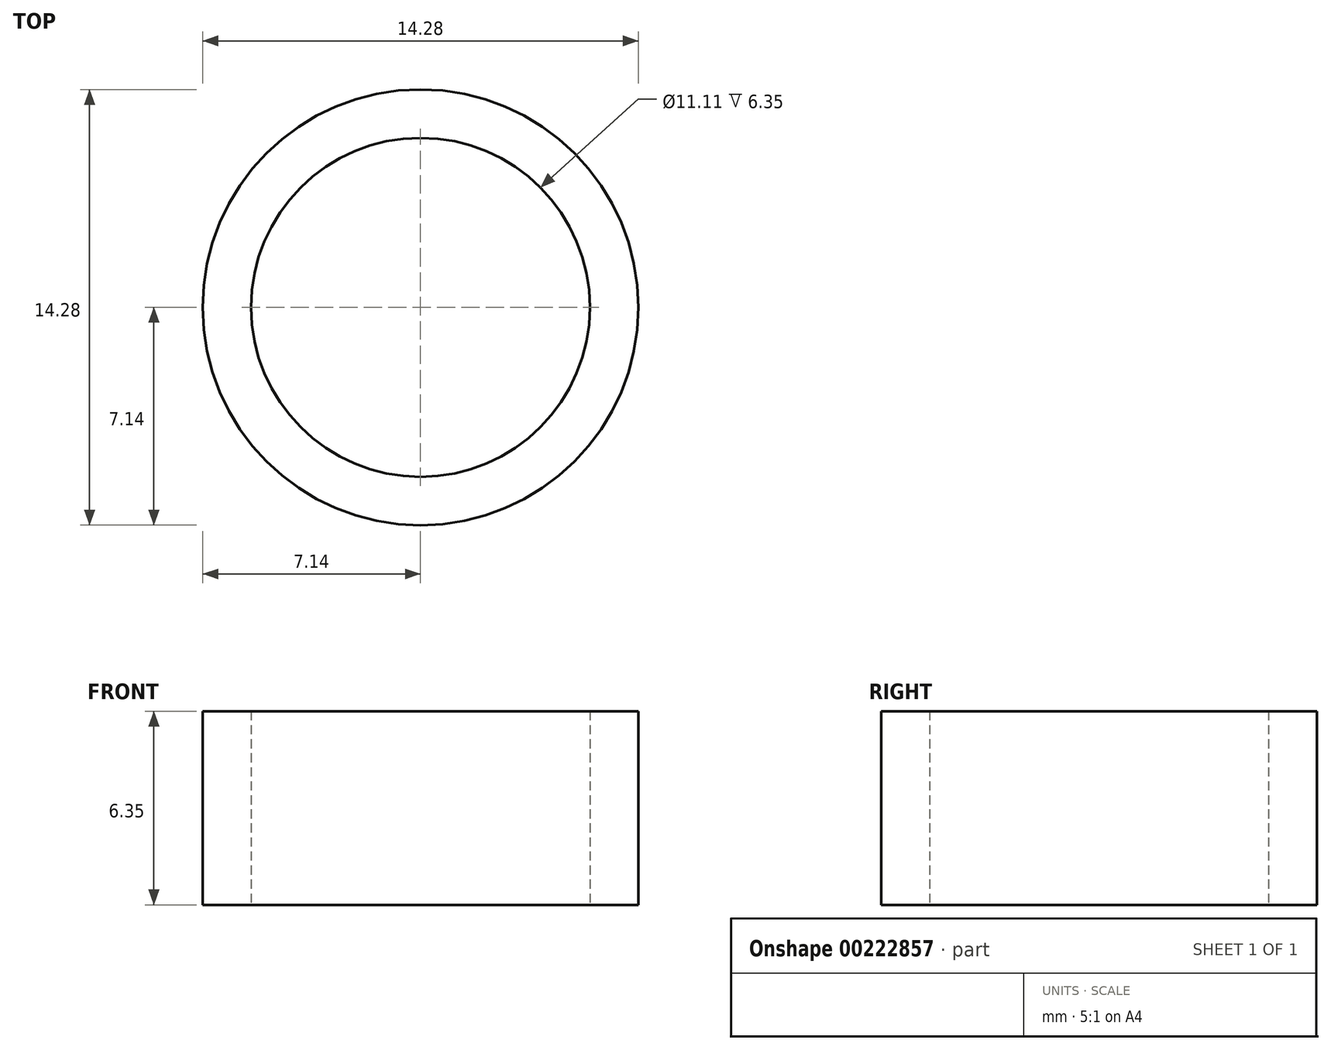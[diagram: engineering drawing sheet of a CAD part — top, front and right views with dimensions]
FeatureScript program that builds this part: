
annotation { "Feature Type Name" : "Feature", "Feature Type Description" : "" }
export const myFeature = defineFeature(function(context is Context, id is Id, definition is map)
    precondition{}
    {
        {
            var Q0;
            Q0=qCreatedBy(makeId("Top.planeOp"),FACE);
            var sketch = newSketch(context, id + "F0", { "sketchPlane" : qUnion([Q0])});
            skCircle(sketch, "E0", {"center": v(0, 0) * mm, "radius": 7.14 * mm});
            skCircle(sketch, "E1", {"center": v(0, 0) * mm, "radius": 5.56 * mm});
            skSolve(sketch);
        }
        {
            var Q0;
            Q0=qSketchRegion(id+"F0",true);
            extrude(context, id + "F1", {"entities" : qUnion([Q0]), "depth" : 6.35 * mm});
        }
    });
